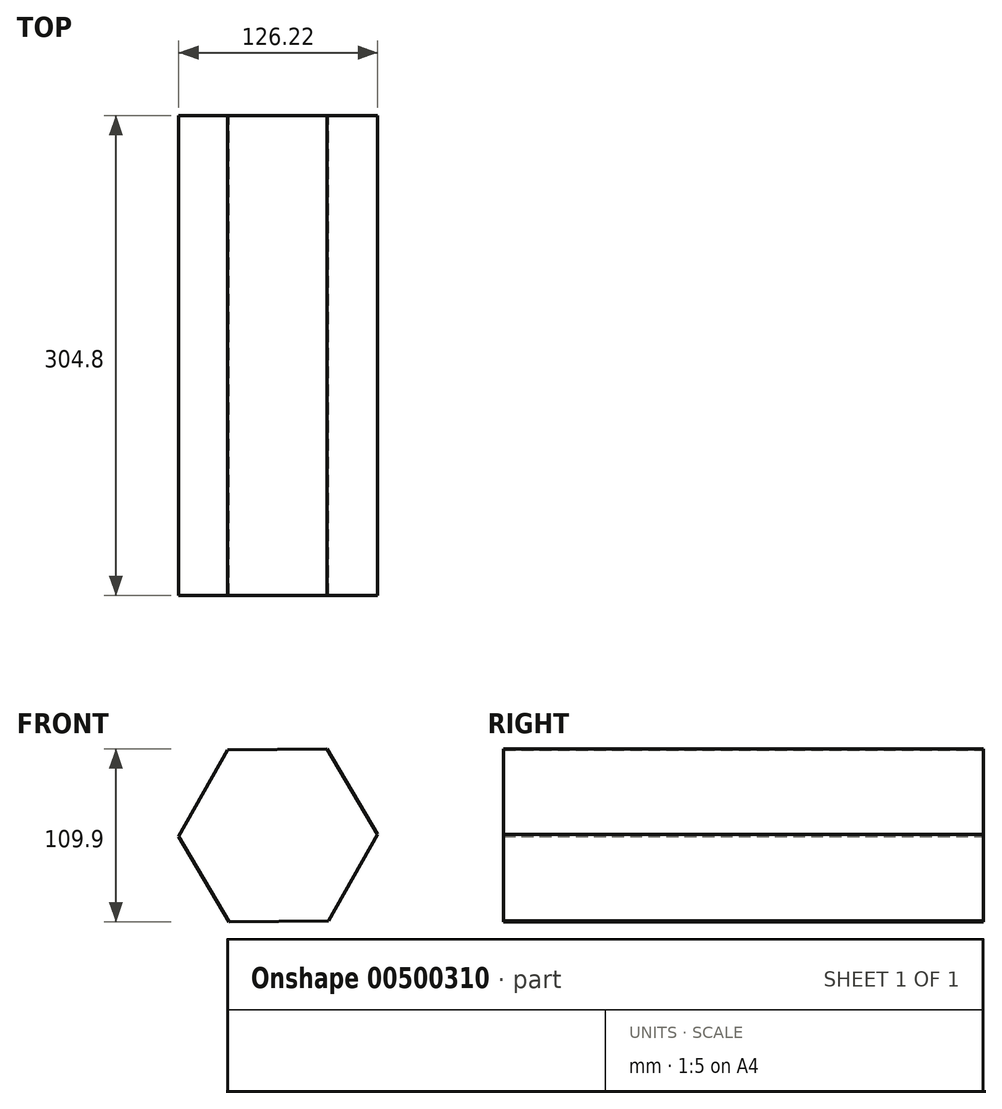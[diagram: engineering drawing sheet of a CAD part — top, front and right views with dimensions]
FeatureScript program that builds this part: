
annotation { "Feature Type Name" : "Feature", "Feature Type Description" : "" }
export const myFeature = defineFeature(function(context is Context, id is Id, definition is map)
    precondition{}
    {
        {
            var Q0;
            Q0=qCreatedBy(makeId("Front.planeOp"),FACE);
            var sketch = newSketch(context, id + "F0", { "sketchPlane" : qUnion([Q0])});
            skCircle(sketch, "E0.cCircle", {"center": v(0, 0) * mm, "radius": 63.11 * mm, "construction": true});
            skLineSegment(sketch, "E0.0", {"start": v(-32.06, 54.36) * mm, "end": v(31.05, 54.95) * mm});
            skLineSegment(sketch, "E0.1", {"start": v(31.05, 54.95) * mm, "end": v(63.1, 0.59) * mm});
            skLineSegment(sketch, "E0.2", {"start": v(63.1, 0.59) * mm, "end": v(32.06, -54.36) * mm});
            skLineSegment(sketch, "E0.3", {"start": v(32.06, -54.36) * mm, "end": v(-31.05, -54.95) * mm});
            skLineSegment(sketch, "E0.4", {"start": v(-31.05, -54.95) * mm, "end": v(-63.1, -0.59) * mm});
            skLineSegment(sketch, "E0.5", {"start": v(-63.1, -0.59) * mm, "end": v(-32.06, 54.36) * mm});
            skSolve(sketch);
        }
        {
            var Q0;
            Q0=makeQuery(id+"F0.imprint","IMPRINT",FACE,{"disambiguationData":[TD([[makeQuery(id+"F0.imprint","IMPRINT",EDGE,{"derivedFrom":sQuery(id+"F0.wireOp",EDGE,"E0.0")}),-1.0]])]});
            extrude(context, id + "F1", {"entities" : qUnion([Q0]), "depth" : 304.8 * mm});
        }
    });
